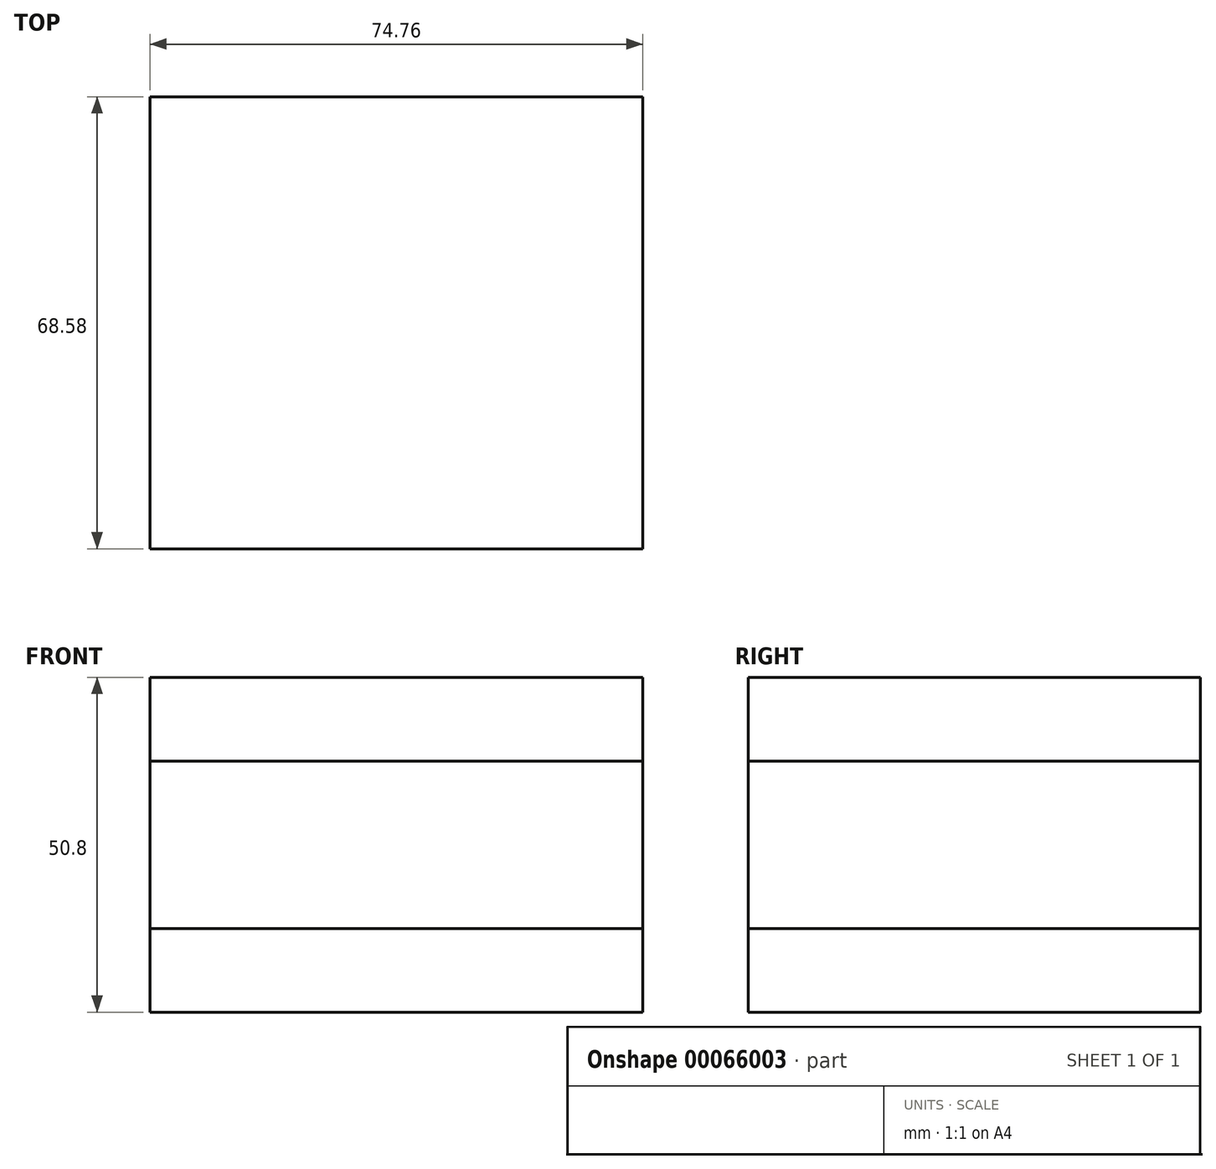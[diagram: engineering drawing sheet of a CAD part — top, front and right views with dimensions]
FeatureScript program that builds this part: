
annotation { "Feature Type Name" : "Feature", "Feature Type Description" : "" }
export const myFeature = defineFeature(function(context is Context, id is Id, definition is map)
    precondition{}
    {
        {
            var Q0;
            Q0=qCreatedBy(makeId("Top.planeOp"),FACE);
            var sketch = newSketch(context, id + "F0", { "sketchPlane" : qUnion([Q0])});
            skLineSegment(sketch, "E0.rect.bottom", {"start": v(-37.38, 34.3) * mm, "end": v(37.38, 34.3) * mm});
            skLineSegment(sketch, "E0.rect.top", {"start": v(-37.38, -34.3) * mm, "end": v(37.38, -34.3) * mm});
            skLineSegment(sketch, "E0.rect.left", {"start": v(-37.38, 34.3) * mm, "end": v(-37.38, -34.3) * mm});
            skLineSegment(sketch, "E0.rect.right", {"start": v(37.38, 34.3) * mm, "end": v(37.38, -34.3) * mm});
            skPoint(sketch, "E0.rect.middle", {"position": v(0, 0) * mm});
            skSolve(sketch);
        }
        {
            var Q0;
            Q0=makeQuery(id+"F0.imprint","IMPRINT",FACE,{"disambiguationData":[TD([[makeQuery(id+"F0.imprint","IMPRINT",EDGE,{"derivedFrom":sQuery(id+"F0.wireOp",EDGE,"E0.rect.bottom")}),-1.0]])]});
            extrude(context, id + "F1", {"entities" : qUnion([Q0]), "endBound" : BoundingType.SYMMETRIC, "depth" : 50.8 * mm});
        }
        {
            var Q0;
            Q0 = qSketchRegion(id + "F0", true);
            extrude(context, id + "F2", {"entities" : qUnion([Q0]), "endBound" : BoundingType.SYMMETRIC, "depth" : 25.4 * mm});
        }
    });
